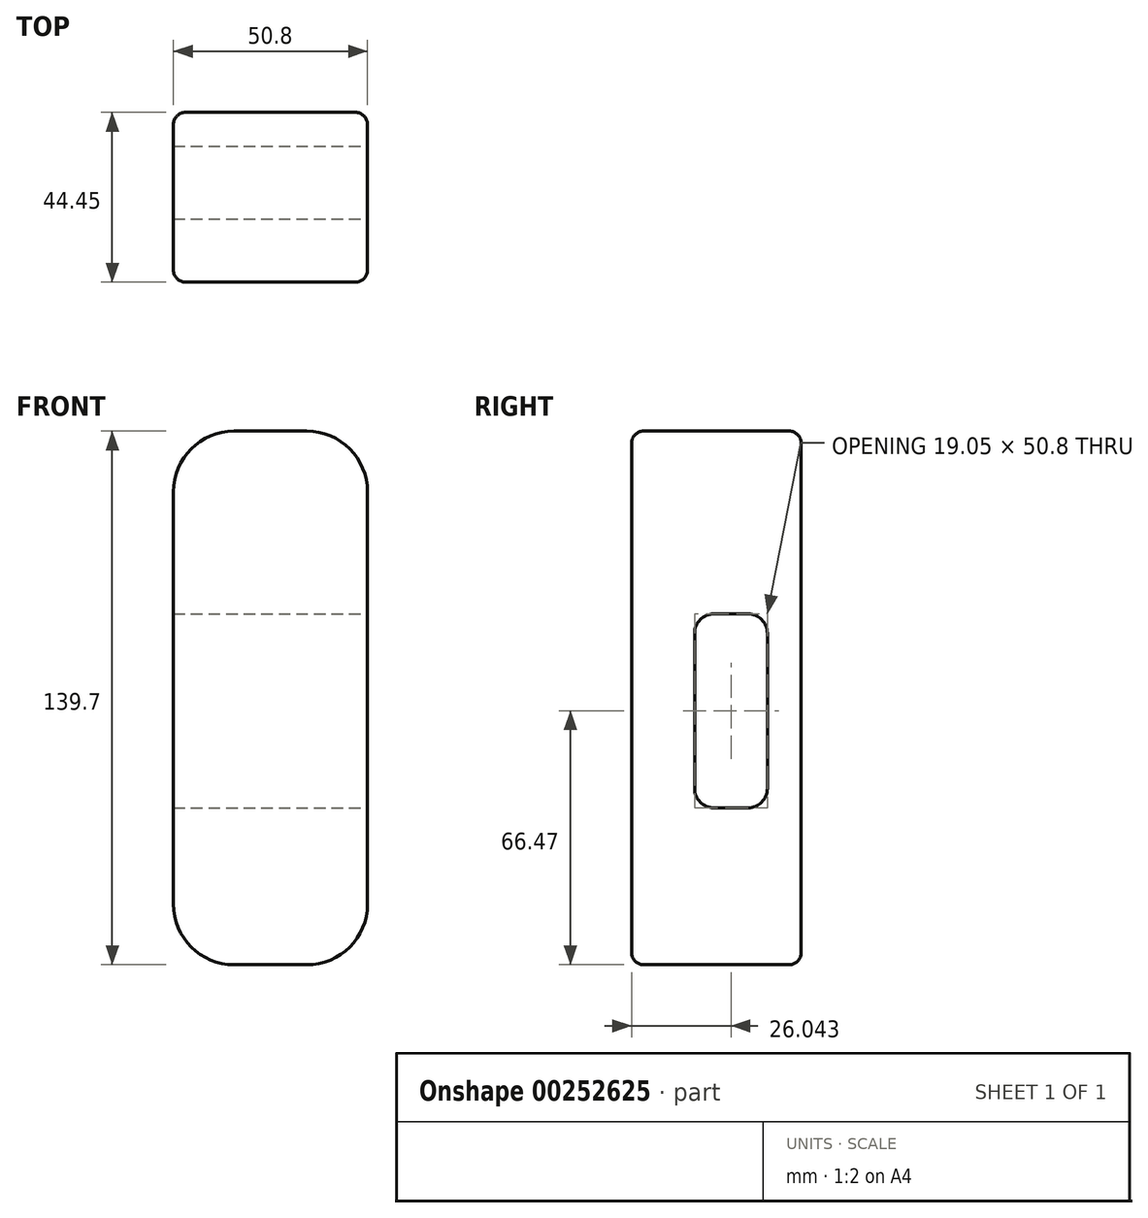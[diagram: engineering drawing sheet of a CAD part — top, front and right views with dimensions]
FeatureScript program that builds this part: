
annotation { "Feature Type Name" : "Feature", "Feature Type Description" : "" }
export const myFeature = defineFeature(function(context is Context, id is Id, definition is map)
    precondition{}
    {
        {
            var Q0;
            Q0=qCreatedBy(makeId("Front.planeOp"),FACE);
            var sketch = newSketch(context, id + "F0", { "sketchPlane" : qUnion([Q0])});
            skLineSegment(sketch, "E0.bottom", {"start": v(9.52, 69.85) * mm, "end": v(-9.53, 69.85) * mm});
            skLineSegment(sketch, "E0.top", {"start": v(9.53, -69.85) * mm, "end": v(-9.52, -69.85) * mm});
            skLineSegment(sketch, "E0.left", {"start": v(25.4, 53.98) * mm, "end": v(25.4, -53.98) * mm});
            skLineSegment(sketch, "E0.right", {"start": v(-25.4, 53.98) * mm, "end": v(-25.4, -53.98) * mm});
            skPoint(sketch, "E0.middle", {"position": v(0, 0) * mm});
            skPoint(sketch, "E1.visualSharp", {"position": v(-25.4, 69.85) * mm});
            skArc(sketch, "E1.filletArc", {"start": v(-15.45, 68.7) * mm, "mid": v(-22.68, 62.86) * mm, "end": v(-25.4, 53.98) * mm});
            skPoint(sketch, "E2.visualSharp", {"position": v(25.4, 69.85) * mm});
            skArc(sketch, "E2.filletArc", {"start": v(25.4, 53.98) * mm, "mid": v(20.75, 65.2) * mm, "end": v(9.52, 69.85) * mm});
            skPoint(sketch, "E3.visualSharp", {"position": v(25.4, -69.85) * mm});
            skArc(sketch, "E3.filletArc", {"start": v(9.53, -69.85) * mm, "mid": v(20.75, -65.2) * mm, "end": v(25.4, -53.98) * mm});
            skPoint(sketch, "E4.visualSharp", {"position": v(-25.4, -69.85) * mm});
            skArc(sketch, "E4.filletArc", {"start": v(-25.4, -53.98) * mm, "mid": v(-20.75, -65.2) * mm, "end": v(-9.52, -69.85) * mm});
            skPoint(sketch, "E5.visualSharp", {"position": v(-9.53, 69.85) * mm});
            skArc(sketch, "E5.filletArc", {"start": v(-9.53, 69.85) * mm, "mid": v(-12.54, 69.56) * mm, "end": v(-15.45, 68.7) * mm});
            skSolve(sketch);
        }
        {
            var Q0;
            Q0=makeQuery(id+"F0.imprint","IMPRINT",FACE,{"disambiguationData":[TD([[makeQuery(id+"F0.imprint","IMPRINT",EDGE,{"derivedFrom":sQuery(id+"F0.wireOp",EDGE,"E0.bottom")}),1.0]])]});
            extrude(context, id + "F1", {"entities" : qUnion([Q0]), "depth" : 44.45 * mm});
        }
        {
            var Q0;
            Q0=makeQuery(id+"F1.opExtrude","SWEPT_FACE",FACE,{"disambiguationData":[OSD([sQuery(id+"F0.wireOp",EDGE,"E0.left")])]});
            var sketch = newSketch(context, id + "F2", { "sketchPlane" : qUnion([Q0])});
            skLineSegment(sketch, "E6.bottom", {"start": v(-22.85, 22.02) * mm, "end": v(-13.96, 22.02) * mm});
            skLineSegment(sketch, "E6.top", {"start": v(-22.85, -28.78) * mm, "end": v(-13.96, -28.78) * mm});
            skLineSegment(sketch, "E6.left", {"start": v(-27.93, 16.94) * mm, "end": v(-27.93, -23.7) * mm});
            skLineSegment(sketch, "E6.right", {"start": v(-8.88, 16.94) * mm, "end": v(-8.88, -23.7) * mm});
            skPoint(sketch, "E7.visualSharp", {"position": v(-27.93, 22.02) * mm});
            skArc(sketch, "E7.filletArc", {"start": v(-22.85, 22.02) * mm, "mid": v(-26.44, 20.53) * mm, "end": v(-27.93, 16.94) * mm});
            skPoint(sketch, "E8.visualSharp", {"position": v(-8.88, 22.02) * mm});
            skArc(sketch, "E8.filletArc", {"start": v(-8.88, 16.94) * mm, "mid": v(-10.37, 20.53) * mm, "end": v(-13.96, 22.02) * mm});
            skPoint(sketch, "E9.visualSharp", {"position": v(-27.93, -28.78) * mm});
            skArc(sketch, "E9.filletArc", {"start": v(-27.93, -23.7) * mm, "mid": v(-26.44, -27.3) * mm, "end": v(-22.85, -28.78) * mm});
            skPoint(sketch, "E10.visualSharp", {"position": v(-8.88, -28.78) * mm});
            skArc(sketch, "E10.filletArc", {"start": v(-13.96, -28.78) * mm, "mid": v(-10.37, -27.3) * mm, "end": v(-8.88, -23.7) * mm});
            skSolve(sketch);
        }
        {
            var Q0;
            Q0=makeQuery(id+"F2.imprint","IMPRINT",FACE,{"disambiguationData":[TD([[makeQuery(id+"F2.imprint","IMPRINT",EDGE,{"derivedFrom":sQuery(id+"F2.wireOp",EDGE,"E6.bottom")}),-1.0]])]});
            extrude(context, id + "F3", {"entities" : qUnion([Q0]), "operationType" : NewBodyOperationType.REMOVE, "endBound" : BoundingType.THROUGH_ALL, "oppositeDirection" : true, "depth" : 25.4 * mm});
        }
        {
            var Q0;
            Q0=makeQuery(id+"F1.opExtrude","CAP_EDGE",EDGE,{"disambiguationData":[OSD([sQuery(id+"F0.wireOp",EDGE,"E0.bottom")])],"isStart":false});
            var Q1;
            Q1=makeQuery(id+"F1.opExtrude","CAP_EDGE",EDGE,{"disambiguationData":[OSD([sQuery(id+"F0.wireOp",EDGE,"E0.bottom")])],"isStart":true});
            fillet(context, id + "F4", {"entities" : qUnion([Q0, Q1]), "radius" : 3.17 * mm, "tangentPropagation" : true, "allowEdgeOverflow" : false});
        }
    });
